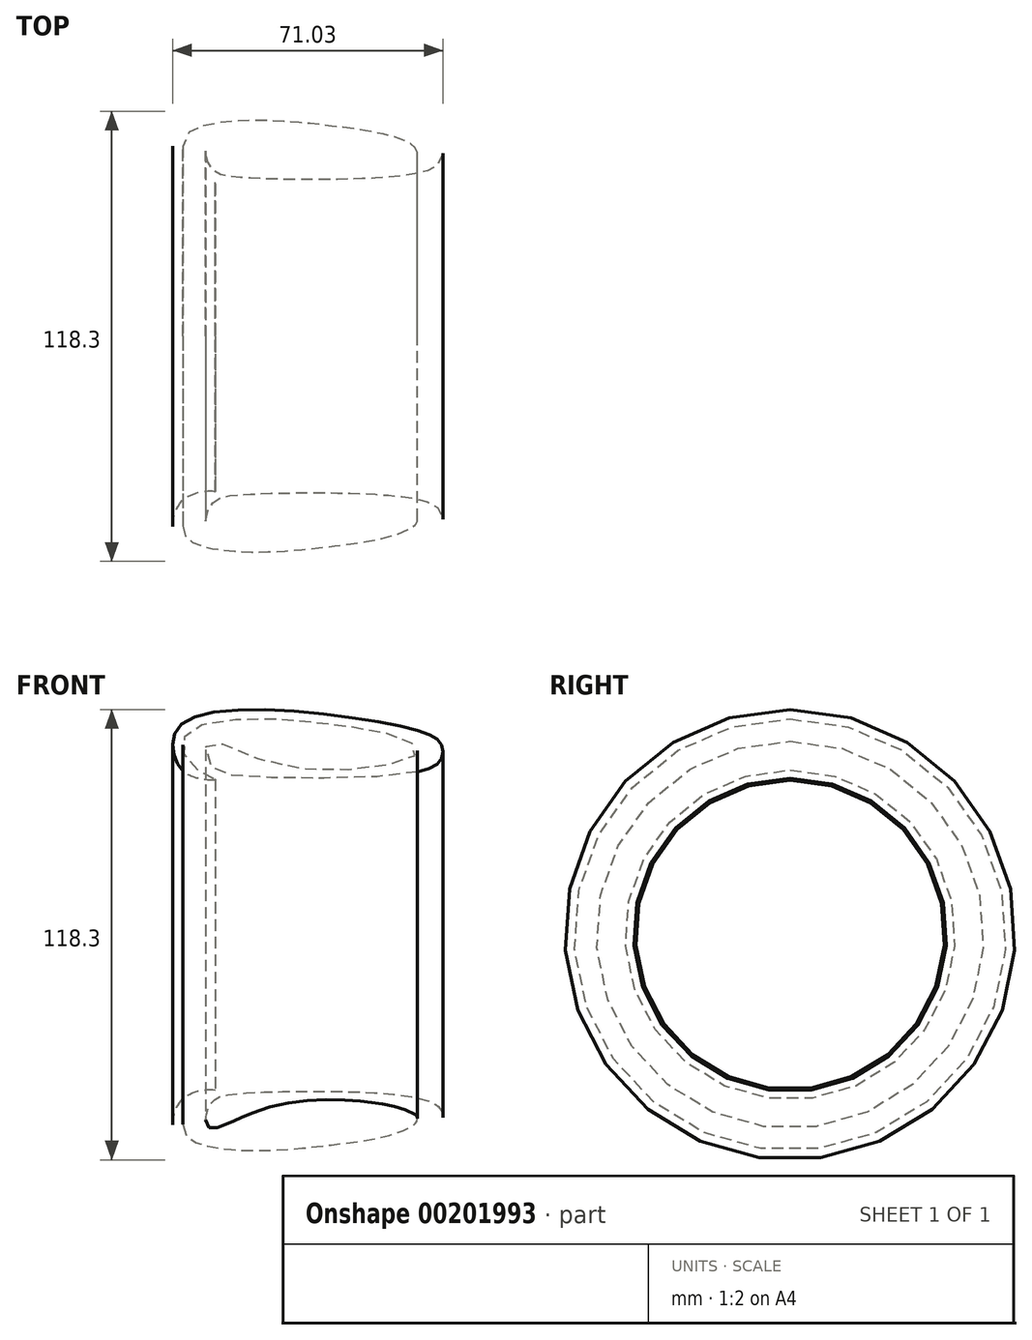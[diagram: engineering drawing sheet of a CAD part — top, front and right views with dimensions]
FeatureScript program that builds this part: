
annotation { "Feature Type Name" : "Feature", "Feature Type Description" : "" }
export const myFeature = defineFeature(function(context is Context, id is Id, definition is map)
    precondition{}
    {
        {
            var Q0;
            Q0=qCreatedBy(makeId("Front.planeOp"),FACE);
            var sketch = newSketch(context, id + "F0", { "sketchPlane" : qUnion([Q0])});
            skFitSpline(sketch, "E0", {"points": [v(-4.96, 40.83) * mm, v(-10.4, 41.34) * mm, v(-15.54, 46.48) * mm, v(-12.62, 56.25) * mm, v(44.82, 54.54) * mm, v(54.5, 49.8) * mm, v(54.09, 45.67) * mm, v(41.19, 41.84) * mm, v(2, 41.64) * mm, v(-6.27, 44.56) * mm, v(-6.87, 50.5) * mm, v(8.04, 45.67) * mm, v(38.77, 44.46) * mm, v(48.14, 48.09) * mm, v(44.82, 51.31) * mm, v(25.47, 55.24) * mm, v(2.9, 56.65) * mm, v(-12.01, 53.43) * mm, v(-13.42, 49.3) * mm, v(-11, 44.16) * mm, v(-4.96, 40.83) * mm]});
            skLineSegment(sketch, "E1", {"start": v(0, 0) * mm, "end": v(125.78, 0) * mm, "construction": true});
            skSolve(sketch);
        }
        {
            var Q0;
            Q0=makeQuery(id+"F0.imprint","IMPRINT",FACE,{"disambiguationData":[TD([[makeQuery(id+"F0.imprint","IMPRINT",EDGE,{"derivedFrom":sQuery(id+"F0.wireOp",EDGE,"E0")}),-1.0]])]});
            var Q1;
            Q1=sQuery(id+"F0.wireOp",EDGE,"E1");
            revolve(context, id + "F1", {"entities" : qUnion([Q0]), "axis" : qUnion([Q1]), "revolveType" : RevolveType.FULL});
        }
    });
